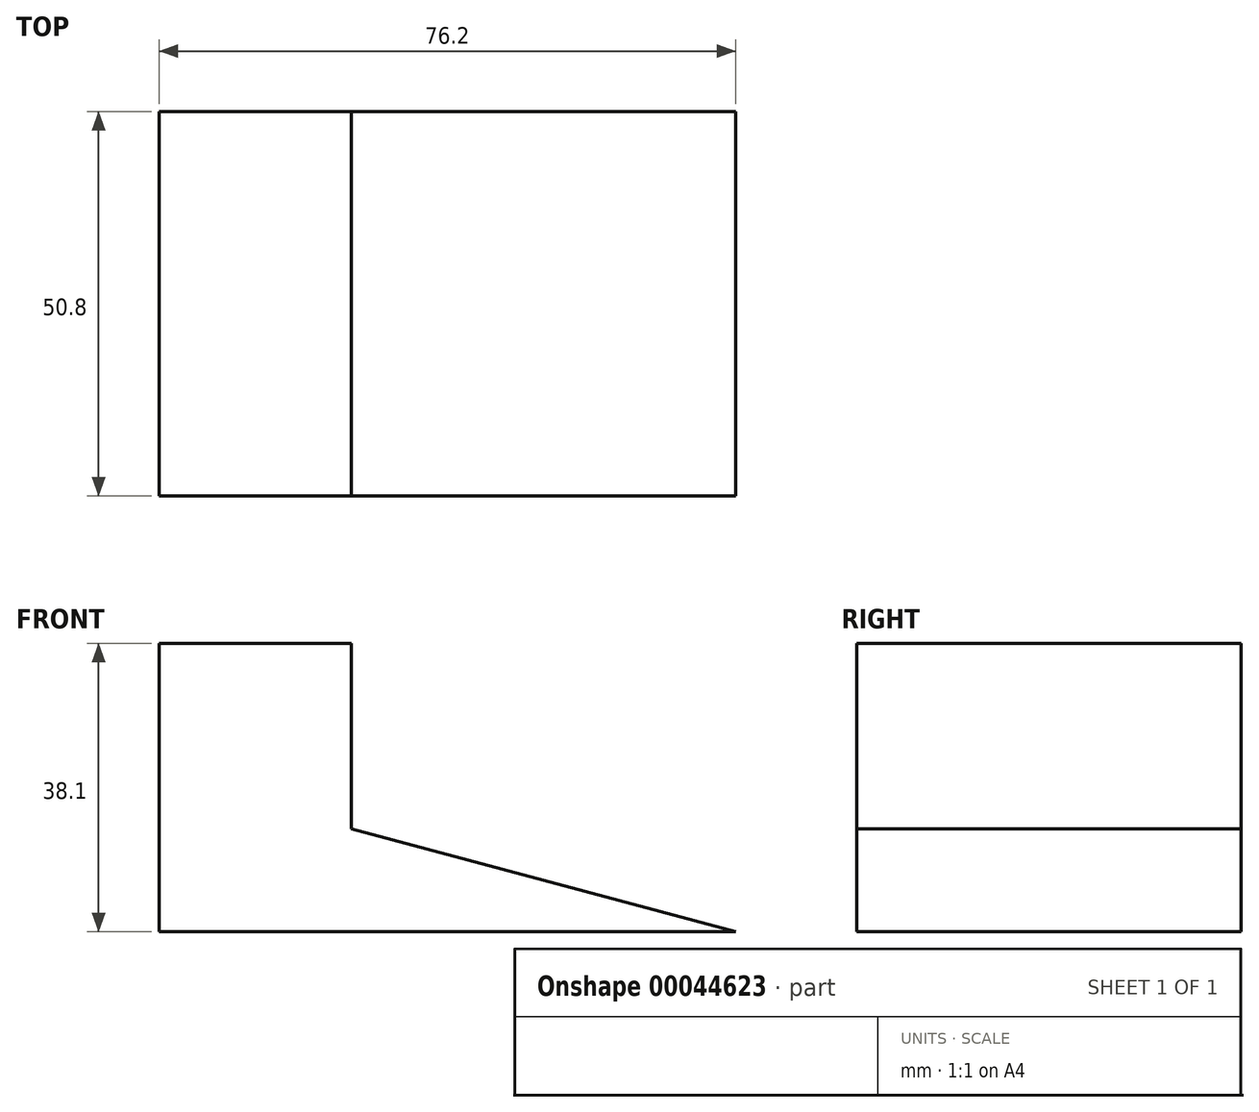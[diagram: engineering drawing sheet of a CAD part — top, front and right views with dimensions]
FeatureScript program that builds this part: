
annotation { "Feature Type Name" : "Feature", "Feature Type Description" : "" }
export const myFeature = defineFeature(function(context is Context, id is Id, definition is map)
    precondition{}
    {
        {
            var Q0;
            Q0=qCreatedBy(makeId("Front.planeOp"),FACE);
            var sketch = newSketch(context, id + "F0", { "sketchPlane" : qUnion([Q0])});
            skLineSegment(sketch, "E0", {"start": v(0, 0) * mm, "end": v(76.2, 0) * mm});
            skLineSegment(sketch, "E1", {"start": v(76.2, 0) * mm, "end": v(25.4, 13.61) * mm});
            skLineSegment(sketch, "E2", {"start": v(25.4, 13.61) * mm, "end": v(25.4, 38.1) * mm});
            skLineSegment(sketch, "E3", {"start": v(25.4, 38.1) * mm, "end": v(0, 38.1) * mm});
            skLineSegment(sketch, "E4", {"start": v(0, 38.1) * mm, "end": v(0, 0) * mm});
            skSolve(sketch);
        }
        {
            var Q0;
            Q0=makeQuery(id+"F0.imprint","IMPRINT",FACE,{"disambiguationData":[TD([[makeQuery(id+"F0.imprint","IMPRINT",EDGE,{"derivedFrom":sQuery(id+"F0.wireOp",EDGE,"E0")}),1.0]])]});
            extrude(context, id + "F1", {"entities" : qUnion([Q0]), "depth" : 50.8 * mm, "symmetric" : true});
        }
    });
